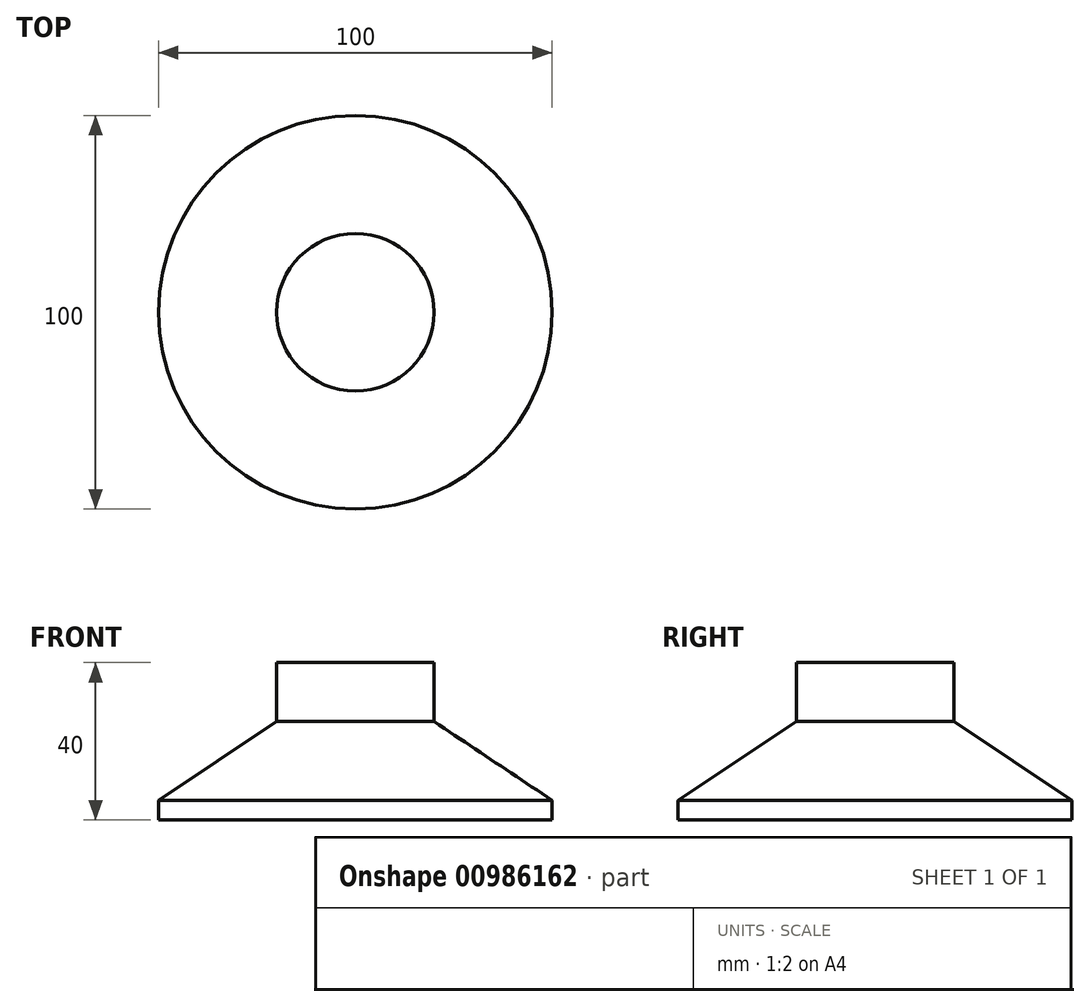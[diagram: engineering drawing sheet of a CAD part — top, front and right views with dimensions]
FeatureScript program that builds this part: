
annotation { "Feature Type Name" : "Feature", "Feature Type Description" : "" }
export const myFeature = defineFeature(function(context is Context, id is Id, definition is map)
    precondition{}
    {
        {
            var Q0;
            Q0=qCreatedBy(makeId("Top.planeOp"),FACE);
            var sketch = newSketch(context, id + "F0", { "sketchPlane" : qUnion([Q0])});
            skCircle(sketch, "E0", {"center": v(0, 0) * mm, "radius": 50 * mm});
            skSolve(sketch);
        }
        {
            var Q0;
            Q0=makeQuery(id+"F0.imprint","IMPRINT",FACE,{"disambiguationData":[TD([[makeQuery(id+"F0.imprint","IMPRINT",EDGE,{"derivedFrom":sQuery(id+"F0.wireOp",EDGE,"E0")}),1.0]])]});
            cPlane(context, id + "F1", {"entities" : qUnion([Q0]), "cplaneType" : CPlaneType.OFFSET, "offset" : 20 * mm, "width" : 150 * mm, "height" : 150 * mm});
        }
        {
            var Q0;
            Q0=qCreatedBy(id+"F1.planeOp",FACE);
            var sketch = newSketch(context, id + "F2", { "sketchPlane" : qUnion([Q0])});
            skCircle(sketch, "E1", {"center": v(0, 0) * mm, "radius": 20 * mm});
            skSolve(sketch);
        }
        {
            var Q0;
            Q0=makeQuery(id+"F0.imprint","IMPRINT",FACE,{"disambiguationData":[TD([[makeQuery(id+"F0.imprint","IMPRINT",EDGE,{"derivedFrom":sQuery(id+"F0.wireOp",EDGE,"E0")}),1.0]])]});
            var Q1;
            Q1=makeQuery(id+"F2.imprint","IMPRINT",FACE,{"disambiguationData":[TD([[makeQuery(id+"F2.imprint","IMPRINT",EDGE,{"derivedFrom":sQuery(id+"F2.wireOp",EDGE,"E1")}),1.0]])]});
            loft(context, id + "F3", {"sheetProfilesArray" : [{ "sheetProfileEntities" : qUnion([Q0]) }, { "sheetProfileEntities" : qUnion([Q1]) }]});
        }
        {
            var Q0;
            Q0=makeQuery(id+"F3.opLoft","CAP_FACE",FACE,{"disambiguationData":[OSD([makeQuery(id+"F2.imprint","IMPRINT",FACE,{"disambiguationData":[TD([[makeQuery(id+"F2.imprint","IMPRINT",EDGE,{"derivedFrom":sQuery(id+"F2.wireOp",EDGE,"E1")}),1.0]])]})])],"isStart":true});
            extrude(context, id + "F4", {"entities" : qUnion([Q0]), "operationType" : NewBodyOperationType.ADD, "depth" : 15 * mm, "offsetDistance" : 25 * mm});
        }
        {
            var Q0;
            Q0=makeQuery(id+"F3.opLoft","CAP_FACE",FACE,{"disambiguationData":[OSD([makeQuery(id+"F0.imprint","IMPRINT",FACE,{"disambiguationData":[TD([[makeQuery(id+"F0.imprint","IMPRINT",EDGE,{"derivedFrom":sQuery(id+"F0.wireOp",EDGE,"E0")}),1.0]])]})])],"isStart":true});
            extrude(context, id + "F5", {"entities" : qUnion([Q0]), "operationType" : NewBodyOperationType.ADD, "depth" : 5 * mm, "offsetDistance" : 25 * mm});
        }
    });
